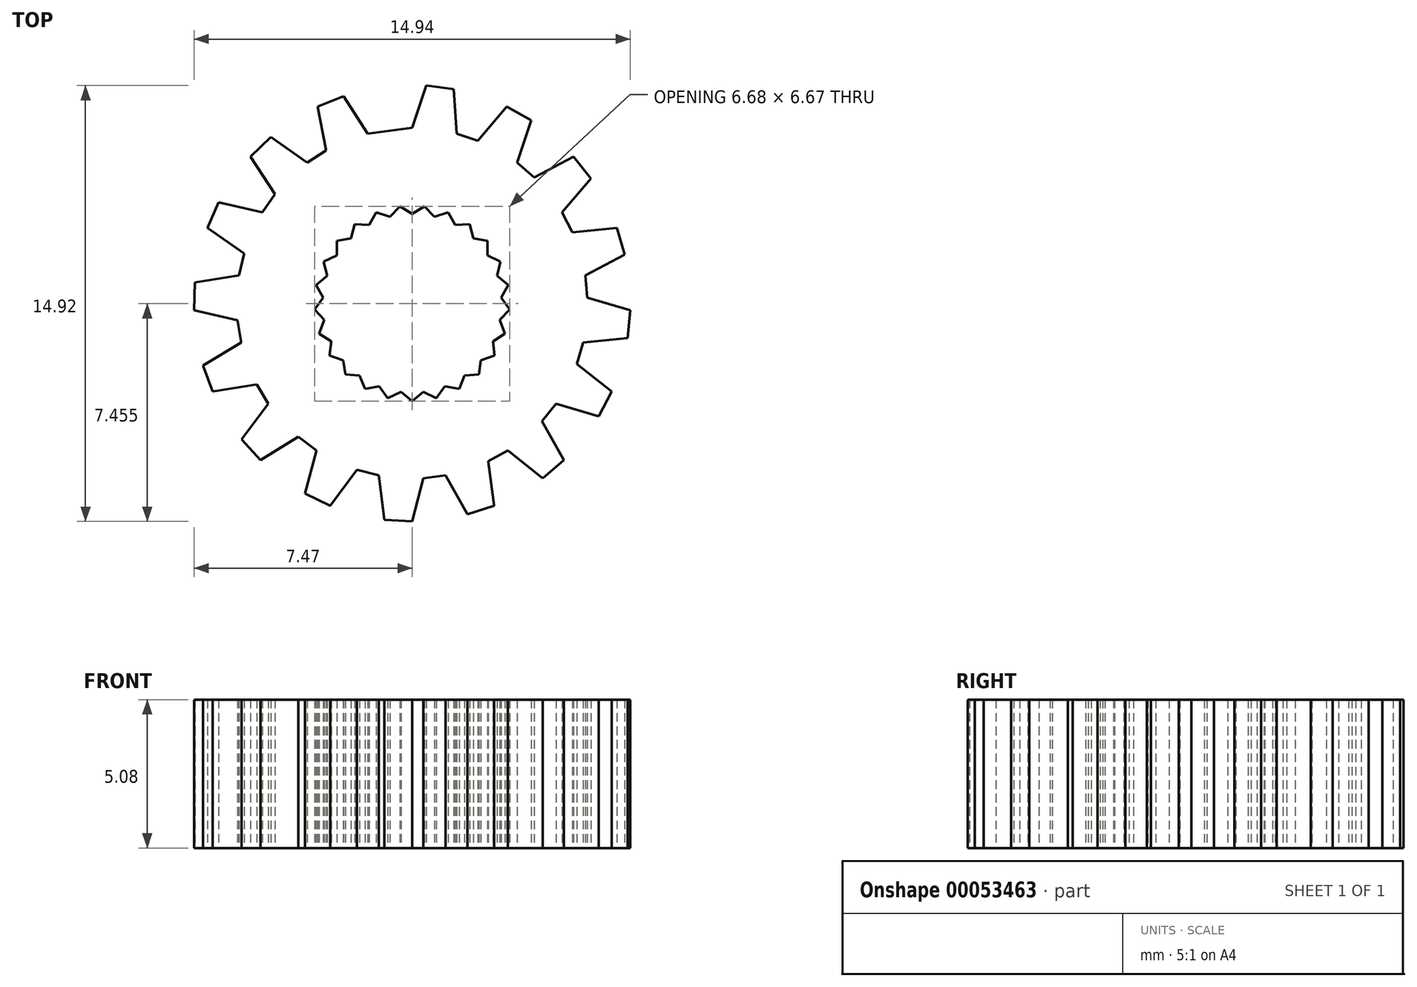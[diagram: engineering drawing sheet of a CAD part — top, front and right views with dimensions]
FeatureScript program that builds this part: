
annotation { "Feature Type Name" : "Feature", "Feature Type Description" : "" }
export const myFeature = defineFeature(function(context is Context, id is Id, definition is map)
    precondition{}
    {
        {
            var Q0;
            Q0=qCreatedBy(makeId("Top.planeOp"),FACE);
            var sketch = newSketch(context, id + "F0", { "sketchPlane" : qUnion([Q0])});
            skLineSegment(sketch, "E0", {"start": v(-0.76, 2.97) * mm, "end": v(-0.42, 3.33) * mm});
            skLineSegment(sketch, "E1", {"start": v(-0.42, 3.33) * mm, "end": v(0, 3.07) * mm});
            skLineSegment(sketch, "E2", {"start": v(-1.47, 2.69) * mm, "end": v(-1.23, 3.12) * mm});
            skLineSegment(sketch, "E3", {"start": v(-1.23, 3.12) * mm, "end": v(-0.76, 2.97) * mm});
            skLineSegment(sketch, "E4", {"start": v(-2.1, 2.24) * mm, "end": v(-1.97, 2.71) * mm});
            skLineSegment(sketch, "E5", {"start": v(-1.97, 2.71) * mm, "end": v(-1.47, 2.69) * mm});
            skLineSegment(sketch, "E6", {"start": v(-2.58, 1.65) * mm, "end": v(-2.58, 2.14) * mm});
            skLineSegment(sketch, "E7", {"start": v(-2.58, 2.14) * mm, "end": v(-2.1, 2.24) * mm});
            skLineSegment(sketch, "E8", {"start": v(-2.9, 0.95) * mm, "end": v(-3.03, 1.43) * mm});
            skLineSegment(sketch, "E9", {"start": v(-3.03, 1.43) * mm, "end": v(-2.58, 1.65) * mm});
            skLineSegment(sketch, "E10", {"start": v(-3.05, 0.2) * mm, "end": v(-3.29, 0.63) * mm});
            skLineSegment(sketch, "E11", {"start": v(-3.29, 0.63) * mm, "end": v(-2.9, 0.95) * mm});
            skLineSegment(sketch, "E12", {"start": v(-3, -0.57) * mm, "end": v(-3.34, -0.2) * mm});
            skLineSegment(sketch, "E13", {"start": v(-3.34, -0.2) * mm, "end": v(-3.05, 0.2) * mm});
            skLineSegment(sketch, "E14", {"start": v(-2.77, -1.3) * mm, "end": v(-3.18, -1.03) * mm});
            skLineSegment(sketch, "E15", {"start": v(-3.18, -1.03) * mm, "end": v(-3, -0.57) * mm});
            skLineSegment(sketch, "E16", {"start": v(-2.36, -1.94) * mm, "end": v(-2.83, -1.79) * mm});
            skLineSegment(sketch, "E17", {"start": v(-2.83, -1.79) * mm, "end": v(-2.77, -1.3) * mm});
            skLineSegment(sketch, "E18", {"start": v(-1.8, -2.47) * mm, "end": v(-2.3, -2.43) * mm});
            skLineSegment(sketch, "E19", {"start": v(-2.3, -2.43) * mm, "end": v(-2.36, -1.94) * mm});
            skLineSegment(sketch, "E20", {"start": v(-1.13, -2.84) * mm, "end": v(-1.61, -2.92) * mm});
            skLineSegment(sketch, "E21", {"start": v(-1.61, -2.92) * mm, "end": v(-1.8, -2.47) * mm});
            skLineSegment(sketch, "E22", {"start": v(-0.38, -3.03) * mm, "end": v(-0.83, -3.23) * mm});
            skLineSegment(sketch, "E23", {"start": v(-0.83, -3.23) * mm, "end": v(-1.13, -2.84) * mm});
            skLineSegment(sketch, "E24", {"start": v(0.38, -3.03) * mm, "end": v(0, -3.34) * mm});
            skLineSegment(sketch, "E25", {"start": v(0, -3.34) * mm, "end": v(-0.38, -3.03) * mm});
            skLineSegment(sketch, "E26", {"start": v(1.13, -2.84) * mm, "end": v(0.83, -3.23) * mm});
            skLineSegment(sketch, "E27", {"start": v(0.83, -3.23) * mm, "end": v(0.38, -3.03) * mm});
            skLineSegment(sketch, "E28", {"start": v(1.8, -2.47) * mm, "end": v(1.61, -2.92) * mm});
            skLineSegment(sketch, "E29", {"start": v(1.61, -2.92) * mm, "end": v(1.13, -2.84) * mm});
            skLineSegment(sketch, "E30", {"start": v(2.36, -1.94) * mm, "end": v(2.3, -2.43) * mm});
            skLineSegment(sketch, "E31", {"start": v(2.3, -2.43) * mm, "end": v(1.8, -2.47) * mm});
            skLineSegment(sketch, "E32", {"start": v(2.77, -1.3) * mm, "end": v(2.83, -1.79) * mm});
            skLineSegment(sketch, "E33", {"start": v(2.83, -1.79) * mm, "end": v(2.36, -1.94) * mm});
            skLineSegment(sketch, "E34", {"start": v(3, -0.57) * mm, "end": v(3.18, -1.03) * mm});
            skLineSegment(sketch, "E35", {"start": v(3.18, -1.03) * mm, "end": v(2.77, -1.3) * mm});
            skLineSegment(sketch, "E36", {"start": v(3.05, 0.2) * mm, "end": v(3.34, -0.2) * mm});
            skLineSegment(sketch, "E37", {"start": v(3.34, -0.2) * mm, "end": v(3, -0.57) * mm});
            skLineSegment(sketch, "E38", {"start": v(2.9, 0.95) * mm, "end": v(3.29, 0.63) * mm});
            skLineSegment(sketch, "E39", {"start": v(3.29, 0.63) * mm, "end": v(3.05, 0.2) * mm});
            skLineSegment(sketch, "E40", {"start": v(2.58, 1.65) * mm, "end": v(3.03, 1.43) * mm});
            skLineSegment(sketch, "E41", {"start": v(3.03, 1.43) * mm, "end": v(2.9, 0.95) * mm});
            skLineSegment(sketch, "E42", {"start": v(2.1, 2.24) * mm, "end": v(2.58, 2.14) * mm});
            skLineSegment(sketch, "E43", {"start": v(2.58, 2.14) * mm, "end": v(2.58, 1.65) * mm});
            skLineSegment(sketch, "E44", {"start": v(1.47, 2.69) * mm, "end": v(1.97, 2.71) * mm});
            skLineSegment(sketch, "E45", {"start": v(1.97, 2.71) * mm, "end": v(2.1, 2.24) * mm});
            skLineSegment(sketch, "E46", {"start": v(0.76, 2.97) * mm, "end": v(1.23, 3.12) * mm});
            skLineSegment(sketch, "E47", {"start": v(1.23, 3.12) * mm, "end": v(1.47, 2.69) * mm});
            skLineSegment(sketch, "E48", {"start": v(0, 3.07) * mm, "end": v(0.42, 3.33) * mm});
            skLineSegment(sketch, "E49", {"start": v(0.42, 3.33) * mm, "end": v(0.76, 2.97) * mm});
            skLineSegment(sketch, "E50", {"start": v(0, 6.01) * mm, "end": v(0.48, 7.46) * mm});
            skLineSegment(sketch, "E51", {"start": v(0.48, 7.46) * mm, "end": v(1.43, 7.34) * mm});
            skLineSegment(sketch, "E52", {"start": v(1.43, 7.34) * mm, "end": v(1.52, 5.82) * mm});
            skLineSegment(sketch, "E53", {"start": v(2.25, 5.57) * mm, "end": v(3.24, 6.74) * mm});
            skLineSegment(sketch, "E54", {"start": v(3.24, 6.74) * mm, "end": v(4.08, 6.27) * mm});
            skLineSegment(sketch, "E55", {"start": v(4.08, 6.27) * mm, "end": v(3.6, 4.82) * mm});
            skLineSegment(sketch, "E56", {"start": v(3.6, 4.82) * mm, "end": v(4.18, 4.32) * mm});
            skLineSegment(sketch, "E57", {"start": v(4.18, 4.32) * mm, "end": v(5.53, 5.03) * mm});
            skLineSegment(sketch, "E58", {"start": v(5.53, 5.03) * mm, "end": v(6.13, 4.28) * mm});
            skLineSegment(sketch, "E59", {"start": v(6.13, 4.28) * mm, "end": v(5.13, 3.12) * mm});
            skLineSegment(sketch, "E60", {"start": v(5.13, 3.12) * mm, "end": v(5.5, 2.44) * mm});
            skLineSegment(sketch, "E61", {"start": v(5.5, 2.44) * mm, "end": v(7.01, 2.59) * mm});
            skLineSegment(sketch, "E62", {"start": v(7.01, 2.59) * mm, "end": v(7.28, 1.67) * mm});
            skLineSegment(sketch, "E63", {"start": v(7.28, 1.67) * mm, "end": v(5.93, 0.97) * mm});
            skLineSegment(sketch, "E64", {"start": v(5.93, 0.97) * mm, "end": v(6, 0.2) * mm});
            skLineSegment(sketch, "E65", {"start": v(6, 0.2) * mm, "end": v(7.47, -0.23) * mm});
            skLineSegment(sketch, "E66", {"start": v(7.47, -0.23) * mm, "end": v(7.37, -1.18) * mm});
            skLineSegment(sketch, "E67", {"start": v(7.37, -1.18) * mm, "end": v(5.85, -1.33) * mm});
            skLineSegment(sketch, "E68", {"start": v(5.85, -1.33) * mm, "end": v(5.64, -2.07) * mm});
            skLineSegment(sketch, "E69", {"start": v(5.64, -2.07) * mm, "end": v(6.83, -3.02) * mm});
            skLineSegment(sketch, "E70", {"start": v(6.83, -3.02) * mm, "end": v(6.39, -3.86) * mm});
            skLineSegment(sketch, "E71", {"start": v(6.39, -3.86) * mm, "end": v(4.92, -3.43) * mm});
            skLineSegment(sketch, "E72", {"start": v(4.92, -3.43) * mm, "end": v(4.45, -4.03) * mm});
            skLineSegment(sketch, "E73", {"start": v(4.45, -4.03) * mm, "end": v(5.2, -5.36) * mm});
            skLineSegment(sketch, "E74", {"start": v(5.2, -5.36) * mm, "end": v(4.47, -5.98) * mm});
            skLineSegment(sketch, "E75", {"start": v(4.47, -5.98) * mm, "end": v(3.28, -5.02) * mm});
            skLineSegment(sketch, "E76", {"start": v(3.28, -5.02) * mm, "end": v(2.6, -5.4) * mm});
            skLineSegment(sketch, "E77", {"start": v(2.6, -5.4) * mm, "end": v(2.8, -6.92) * mm});
            skLineSegment(sketch, "E78", {"start": v(2.8, -6.92) * mm, "end": v(1.9, -7.22) * mm});
            skLineSegment(sketch, "E79", {"start": v(1.9, -7.22) * mm, "end": v(1.15, -5.89) * mm});
            skLineSegment(sketch, "E80", {"start": v(1.15, -5.89) * mm, "end": v(0.38, -5.98) * mm});
            skLineSegment(sketch, "E81", {"start": v(0.38, -5.98) * mm, "end": v(0, -7.46) * mm});
            skLineSegment(sketch, "E82", {"start": v(0, -7.46) * mm, "end": v(-0.96, -7.4) * mm});
            skLineSegment(sketch, "E83", {"start": v(-0.96, -7.4) * mm, "end": v(-1.15, -5.89) * mm});
            skLineSegment(sketch, "E84", {"start": v(-1.15, -5.89) * mm, "end": v(-1.9, -5.7) * mm});
            skLineSegment(sketch, "E85", {"start": v(-1.9, -5.7) * mm, "end": v(-2.8, -6.92) * mm});
            skLineSegment(sketch, "E86", {"start": v(-2.8, -6.92) * mm, "end": v(-3.67, -6.5) * mm});
            skLineSegment(sketch, "E87", {"start": v(-3.67, -6.5) * mm, "end": v(-3.28, -5.02) * mm});
            skLineSegment(sketch, "E88", {"start": v(-3.28, -5.02) * mm, "end": v(-3.9, -4.56) * mm});
            skLineSegment(sketch, "E89", {"start": v(-3.9, -4.56) * mm, "end": v(-5.2, -5.36) * mm});
            skLineSegment(sketch, "E90", {"start": v(-5.2, -5.36) * mm, "end": v(-5.84, -4.65) * mm});
            skLineSegment(sketch, "E91", {"start": v(-5.84, -4.65) * mm, "end": v(-4.92, -3.43) * mm});
            skLineSegment(sketch, "E92", {"start": v(-4.92, -3.43) * mm, "end": v(-5.32, -2.77) * mm});
            skLineSegment(sketch, "E93", {"start": v(-5.32, -2.77) * mm, "end": v(-6.83, -3.02) * mm});
            skLineSegment(sketch, "E94", {"start": v(-6.83, -3.02) * mm, "end": v(-7.16, -2.12) * mm});
            skLineSegment(sketch, "E95", {"start": v(-7.16, -2.12) * mm, "end": v(-5.85, -1.33) * mm});
            skLineSegment(sketch, "E96", {"start": v(-5.85, -1.33) * mm, "end": v(-5.98, -0.57) * mm});
            skLineSegment(sketch, "E97", {"start": v(-5.98, -0.57) * mm, "end": v(-7.47, -0.23) * mm});
            skLineSegment(sketch, "E98", {"start": v(-7.47, -0.23) * mm, "end": v(-7.44, 0.72) * mm});
            skLineSegment(sketch, "E99", {"start": v(-7.44, 0.72) * mm, "end": v(-5.93, 0.97) * mm});
            skLineSegment(sketch, "E100", {"start": v(-5.93, 0.97) * mm, "end": v(-5.76, 1.72) * mm});
            skLineSegment(sketch, "E101", {"start": v(-5.76, 1.72) * mm, "end": v(-7.01, 2.59) * mm});
            skLineSegment(sketch, "E102", {"start": v(-7.01, 2.59) * mm, "end": v(-6.62, 3.46) * mm});
            skLineSegment(sketch, "E103", {"start": v(-6.62, 3.46) * mm, "end": v(-5.13, 3.12) * mm});
            skLineSegment(sketch, "E104", {"start": v(-5.13, 3.12) * mm, "end": v(-4.7, 3.75) * mm});
            skLineSegment(sketch, "E105", {"start": v(-4.7, 3.75) * mm, "end": v(-5.53, 5.03) * mm});
            skLineSegment(sketch, "E106", {"start": v(-5.53, 5.03) * mm, "end": v(-4.84, 5.7) * mm});
            skLineSegment(sketch, "E107", {"start": v(-4.84, 5.7) * mm, "end": v(-3.6, 4.82) * mm});
            skLineSegment(sketch, "E108", {"start": v(-2.95, 5.24) * mm, "end": v(-3.24, 6.74) * mm});
            skLineSegment(sketch, "E109", {"start": v(-3.24, 6.74) * mm, "end": v(-2.35, 7.1) * mm});
            skLineSegment(sketch, "E110", {"start": v(-2.35, 7.1) * mm, "end": v(-1.52, 5.82) * mm});
            skLineSegment(sketch, "E111", {"start": v(-3.6, 4.82) * mm, "end": v(-2.95, 5.24) * mm});
            skLineSegment(sketch, "E112", {"start": v(-1.52, 5.82) * mm, "end": v(0, 6.01) * mm});
            skLineSegment(sketch, "E113", {"start": v(1.52, 5.82) * mm, "end": v(2.25, 5.57) * mm});
            skSolve(sketch);
        }
        {
            var Q0;
            Q0=makeQuery(id+"F0.imprint","IMPRINT",FACE,{"disambiguationData":[TD([[makeQuery(id+"F0.imprint","IMPRINT",EDGE,{"derivedFrom":sQuery(id+"F0.wireOp",EDGE,"E0")}),1.0]])]});
            extrude(context, id + "F1", {"entities" : qUnion([Q0]), "depth" : 5.08 * mm});
        }
    });
